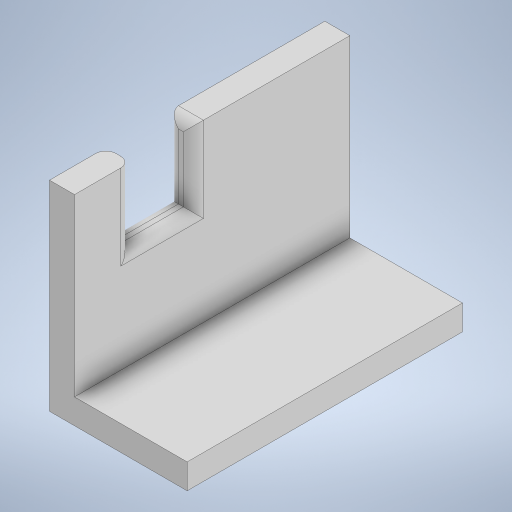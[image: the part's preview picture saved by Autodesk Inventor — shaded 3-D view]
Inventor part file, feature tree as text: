
AUTODESK INVENTOR PART (.ipt)
format: ipt  version: 2023 (Build 270158000, 158)  size: 227,328 bytes
history: native  units: in
note: dims shown in document units (in); Inventor stores cm internally (conversion verified against a paired STEP export)
features: extrude x2, sketch x2, fillet x1
ambient origin geometry x8: Origin, YZ Plane, XZ Plane, XY Plane, X Axis, Y Axis, Z Axis, Center Point
bodies: Solid1 (feature_tree)
feature tree (5):
  extrude  "Extrusion1"  Depth=0.6299in
  extrude  "Extrusion3"  Depth=0.8661in TaperAngle=0.0deg
  fillet  "Fillet1"  Radius=0.1969in
  sketch  "Sketch1"  dims[d0=0.0787in d1=0.6299in]
  sketch  "Sketch3"  dims[d2=0.3543in d3=0.8661in d4=0.0in d9=0.1969in d10=0.2362in d11=0.3937in d12=0.0in d13=0.0315in]
